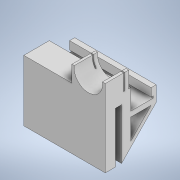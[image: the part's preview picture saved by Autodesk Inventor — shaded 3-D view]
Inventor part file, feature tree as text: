
AUTODESK INVENTOR PART (.ipt)
format: ipt  version: 2020 (Build 240168000, 168)  size: 296,960 bytes
history: native  units: in
note: dims shown in document units (in); Inventor stores cm internally (conversion verified against a paired STEP export)
features: extrude x11, sketch x10, projected_geometry x9, imported_body x1, other x1
ambient origin geometry x8: Origin, YZ Plane, XZ Plane, XY Plane, X Axis, Y Axis, Z Axis, Center Point
bodies: Solid1 (feature_tree)
feature tree (32):
  imported_body  "Base"
  other  "Mount"
  extrude  "Extrusion1"  Depth=1.9685in
  extrude  "Extrusion2"  Depth=2.3622in
  extrude  "Extrusion3"  Depth=0.7874in
  extrude  "Extrusion5"  Depth=0.3937in
  extrude  "Extrusion6"  Depth=0.5906in
  extrude  "Extrusion7"  Depth=0.9055in
  extrude  "Extrusion8"  Depth=3.5433in TaperAngle=0.0deg
  extrude  "Extrusion9"  Depth=0.8976in
  sketch  "Sketch12"  dims[d15=3.5433in d16=0.0in d17=3.5433in d18=0.0in]
  extrude  "Extrusion10"  Depth=0.1969in TaperAngle=0.0deg
  extrude  "Extrusion12"  Depth=0.7087in
  extrude  "Extrusion13"  Depth=0.0394in
  sketch  "Sketch4"  dims[d0=0.2362in d1=1.9685in]
  projected_geometry  "Projected Loop1"
  sketch  "Sketch7"  dims[d2=0.3937in d3=2.3622in]
  projected_geometry  "Projected Loop5"
  sketch  "Sketch8"  dims[d4=0.9843in d5=0.7874in]
  projected_geometry  "Projected Loop6"
  sketch  "Sketch9"  dims[d6=0.7874in d7=0.3937in]
  sketch  "Sketch10"  dims[d8=0.1969in d9=0.5906in]
  sketch  "Sketch11"  dims[d13=0.6299in d14=0.9055in]
  projected_geometry  "Projected Loop7"
  projected_geometry  "Projected Loop8"
  projected_geometry  "Projected Loop9"
  sketch  "Sketch13"  dims[d19=0.1969in d20=0.8976in]
  projected_geometry  "Projected Loop10"
  sketch  "Sketch15"  dims[d21=0.1969in d22=3.5433in d23=0.0in]
  projected_geometry  "Projected Loop14"
  projected_geometry  "Projected Loop15"
  sketch  "Sketch16"  dims[d37=3.5433in d38=0.0in d39=0.7087in d40=0.0394in d41=3.5433in d42=0.0in d44=0.3937in d45=3.5433in d46=0.0in d47=0.315in d48=3.5433in d49=0.0in d50=1.378in d51=0.0in d52=1.0945in d53=0.5472in d54=0.0787in d55=0.0787in d56=0.0in d57=0.0in d58=0.7874in d63=0.5512in d64=1.1024in d65=0.3937in d66=0.0in d67=0.3937in d68=0.0in d69=0.7087in d70=0.2756in d71=0.0197in d72=0.0344in]
